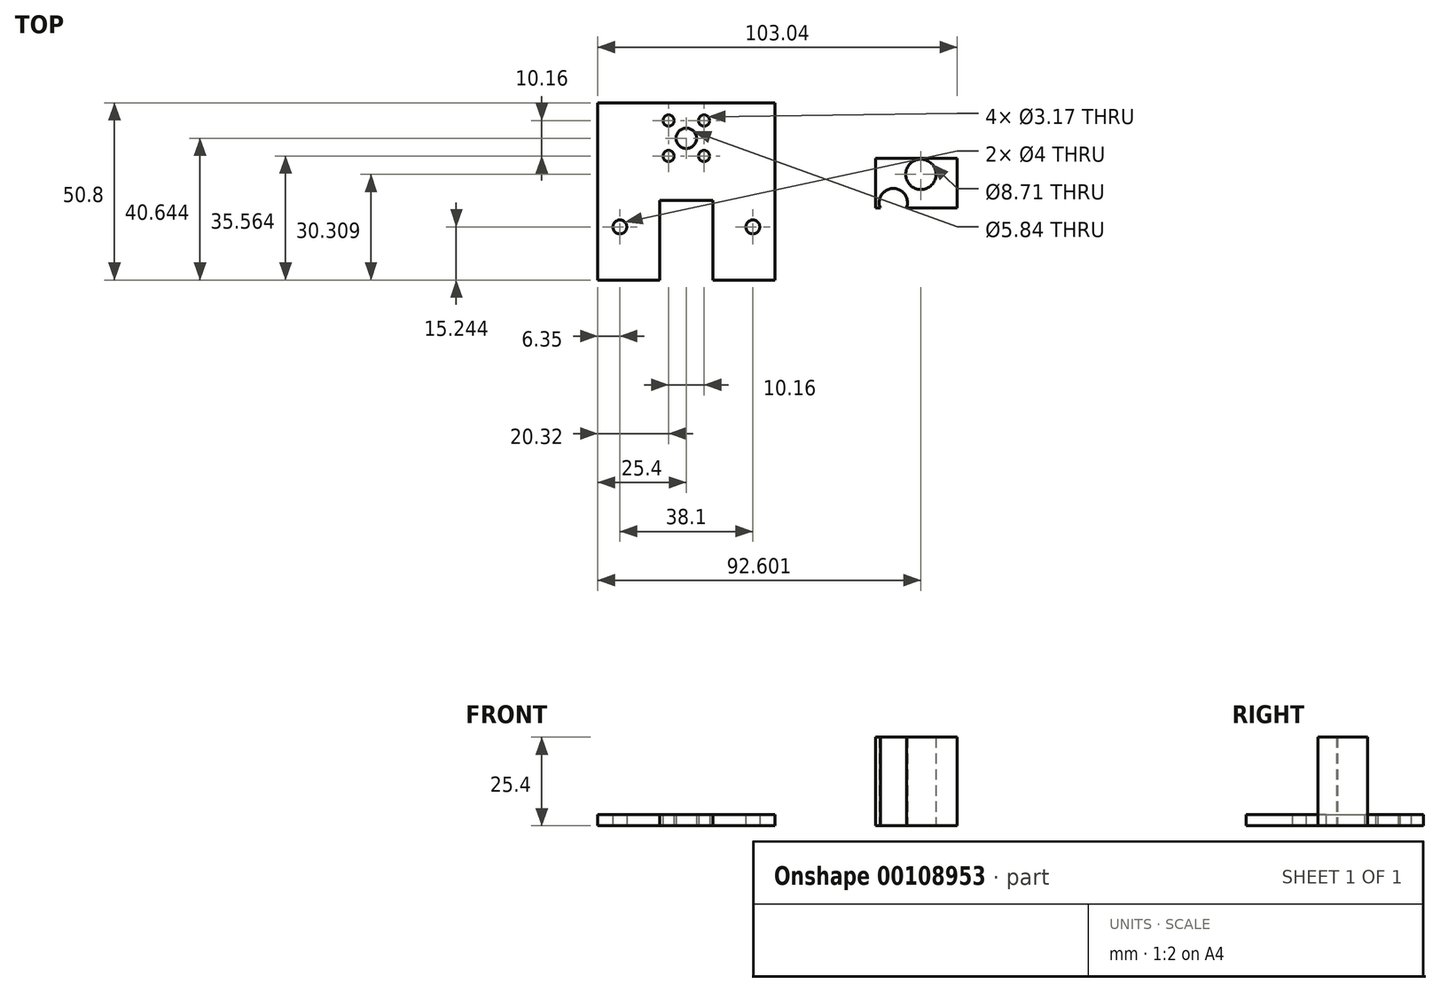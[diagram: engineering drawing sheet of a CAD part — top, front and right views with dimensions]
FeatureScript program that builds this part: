
annotation { "Feature Type Name" : "Feature", "Feature Type Description" : "" }
export const myFeature = defineFeature(function(context is Context, id is Id, definition is map)
    precondition{}
    {
        {
            var Q0;
            Q0=qCreatedBy(makeId("Top.planeOp"),FACE);
            var sketch = newSketch(context, id + "F0", { "sketchPlane" : qUnion([Q0])});
            skLineSegment(sketch, "E0.bottom", {"start": v(-25.4, 25.44) * mm, "end": v(-7.62, 25.44) * mm});
            skLineSegment(sketch, "E0.top", {"start": v(-25.4, 76.24) * mm, "end": v(25.4, 76.24) * mm});
            skLineSegment(sketch, "E0.left", {"start": v(-25.4, 25.44) * mm, "end": v(-25.4, 76.24) * mm});
            skLineSegment(sketch, "E0.right", {"start": v(25.4, 25.44) * mm, "end": v(25.4, 76.24) * mm});
            skCircle(sketch, "E1", {"center": v(0, 66.08) * mm, "radius": 2.92 * mm});
            skCircle(sketch, "E2", {"center": v(-5.08, 71.16) * mm, "radius": 1.59 * mm});
            skCircle(sketch, "E3", {"center": v(-5.08, 61) * mm, "radius": 1.59 * mm});
            skCircle(sketch, "E4", {"center": v(5.08, 71.16) * mm, "radius": 1.59 * mm});
            skCircle(sketch, "E5", {"center": v(5.08, 61) * mm, "radius": 1.59 * mm});
            skLineSegment(sketch, "E6.bottom", {"start": v(-7.62, 48.3) * mm, "end": v(7.62, 48.3) * mm});
            skLineSegment(sketch, "E6.left", {"start": v(-7.62, 48.3) * mm, "end": v(-7.62, 25.44) * mm});
            skLineSegment(sketch, "E6.right", {"start": v(7.62, 48.3) * mm, "end": v(7.62, 25.44) * mm});
            skCircle(sketch, "E7", {"center": v(19.05, 40.68) * mm, "radius": 2 * mm});
            skCircle(sketch, "E8", {"center": v(-19.05, 40.68) * mm, "radius": 2 * mm});
            skPoint(sketch, "E9", {"position": v(0, 76.24) * mm});
            skPoint(sketch, "E10", {"position": v(0, 48.3) * mm});
            skLineSegment(sketch, "E11.trimOffspring", {"start": v(7.62, 25.44) * mm, "end": v(25.4, 25.44) * mm});
            skLineSegment(sketch, "E12.bottom", {"start": v(54.22, 60.33) * mm, "end": v(77.64, 60.33) * mm});
            skLineSegment(sketch, "E12.top", {"start": v(54.22, 46.08) * mm, "end": v(77.64, 46.08) * mm});
            skLineSegment(sketch, "E12.left", {"start": v(54.22, 60.33) * mm, "end": v(54.22, 46.08) * mm});
            skLineSegment(sketch, "E12.right", {"start": v(77.64, 60.33) * mm, "end": v(77.64, 46.08) * mm});
            skCircle(sketch, "E13", {"center": v(59.31, 47.63) * mm, "radius": 4.06 * mm});
            skCircle(sketch, "E14", {"center": v(67.2, 55.75) * mm, "radius": 4.35 * mm});
            skSolve(sketch);
        }
        {
            var Q0;
            Q0=makeQuery(id+"F0.imprint","IMPRINT",FACE,{"disambiguationData":[TD([[makeQuery(id+"F0.imprint","IMPRINT",EDGE,{"derivedFrom":sQuery(id+"F0.wireOp",EDGE,"2006bb52-2d54-4f0e-ba05-1ae574e5513b")}),1.0]])]});
            var Q1;
            Q1=makeQuery(id+"F0.imprint","IMPRINT",FACE,{"disambiguationData":[TD([[makeQuery(id+"F0.imprint","IMPRINT",EDGE,{"derivedFrom":sQuery(id+"F0.wireOp",EDGE,"E0.top")}),-1.0]])]});
            extrude(context, id + "F1", {"entities" : qUnion([Q0, Q1]), "depth" : 3.17 * mm});
        }
        {
            var Q0;
            Q0=makeQuery(id+"F0.imprint","IMPRINT",FACE,{"disambiguationData":[TD([[makeQuery(id+"F0.imprint","IMPRINT",EDGE,{"derivedFrom":sQuery(id+"F0.wireOp",EDGE,"E12.bottom")}),-1.0]])]});
            extrude(context, id + "F2", {"entities" : qUnion([Q0]), "depth" : 25.4 * mm});
        }
    });
